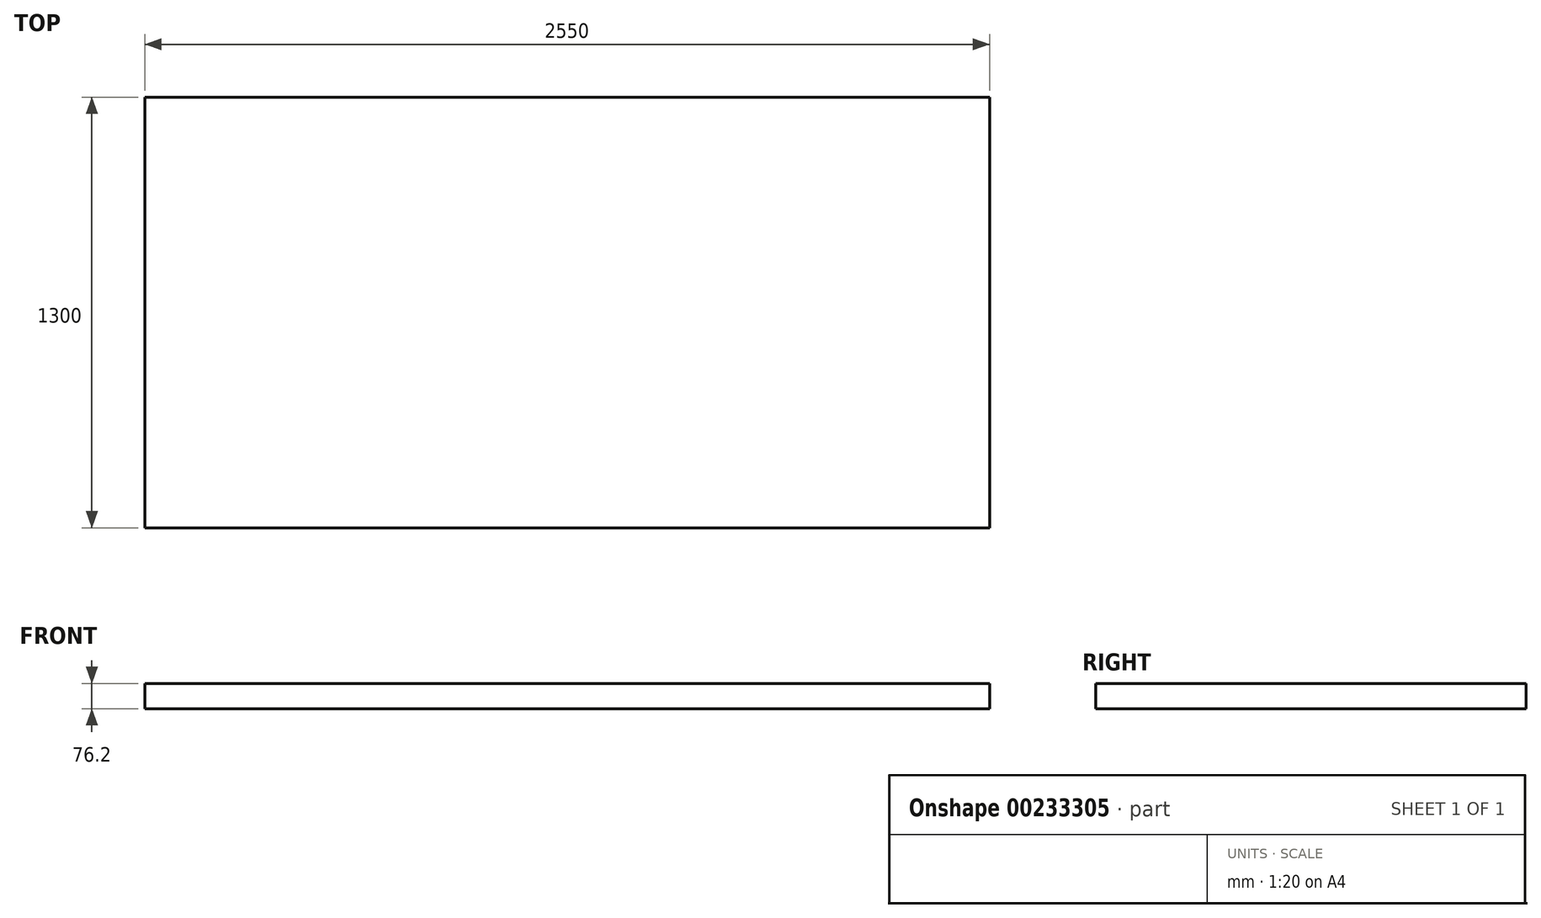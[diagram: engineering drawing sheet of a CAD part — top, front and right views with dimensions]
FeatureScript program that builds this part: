
annotation { "Feature Type Name" : "Feature", "Feature Type Description" : "" }
export const myFeature = defineFeature(function(context is Context, id is Id, definition is map)
    precondition{}
    {
        {
            var Q0;
            Q0=qCreatedBy(makeId("Front.planeOp"),FACE);
            var sketch = newSketch(context, id + "F0", { "sketchPlane" : qUnion([Q0])});
            skLineSegment(sketch, "E0", {"start": v(-1252.49, -266.14) * mm, "end": v(1297.51, -266.14) * mm});
            skLineSegment(sketch, "E1", {"start": v(1297.51, -266.14) * mm, "end": v(1297.51, -342.34) * mm});
            skLineSegment(sketch, "E2", {"start": v(1297.51, -342.34) * mm, "end": v(-1252.49, -342.34) * mm});
            skLineSegment(sketch, "E3", {"start": v(-1252.49, -266.14) * mm, "end": v(-1252.49, -342.34) * mm});
            skSolve(sketch);
        }
        {
            var Q0;
            Q0 = qSketchRegion(id + "F0", true);
            extrude(context, id + "F1", {"entities" : qUnion([Q0]), "depth" : 1300 * mm});
        }
    });
